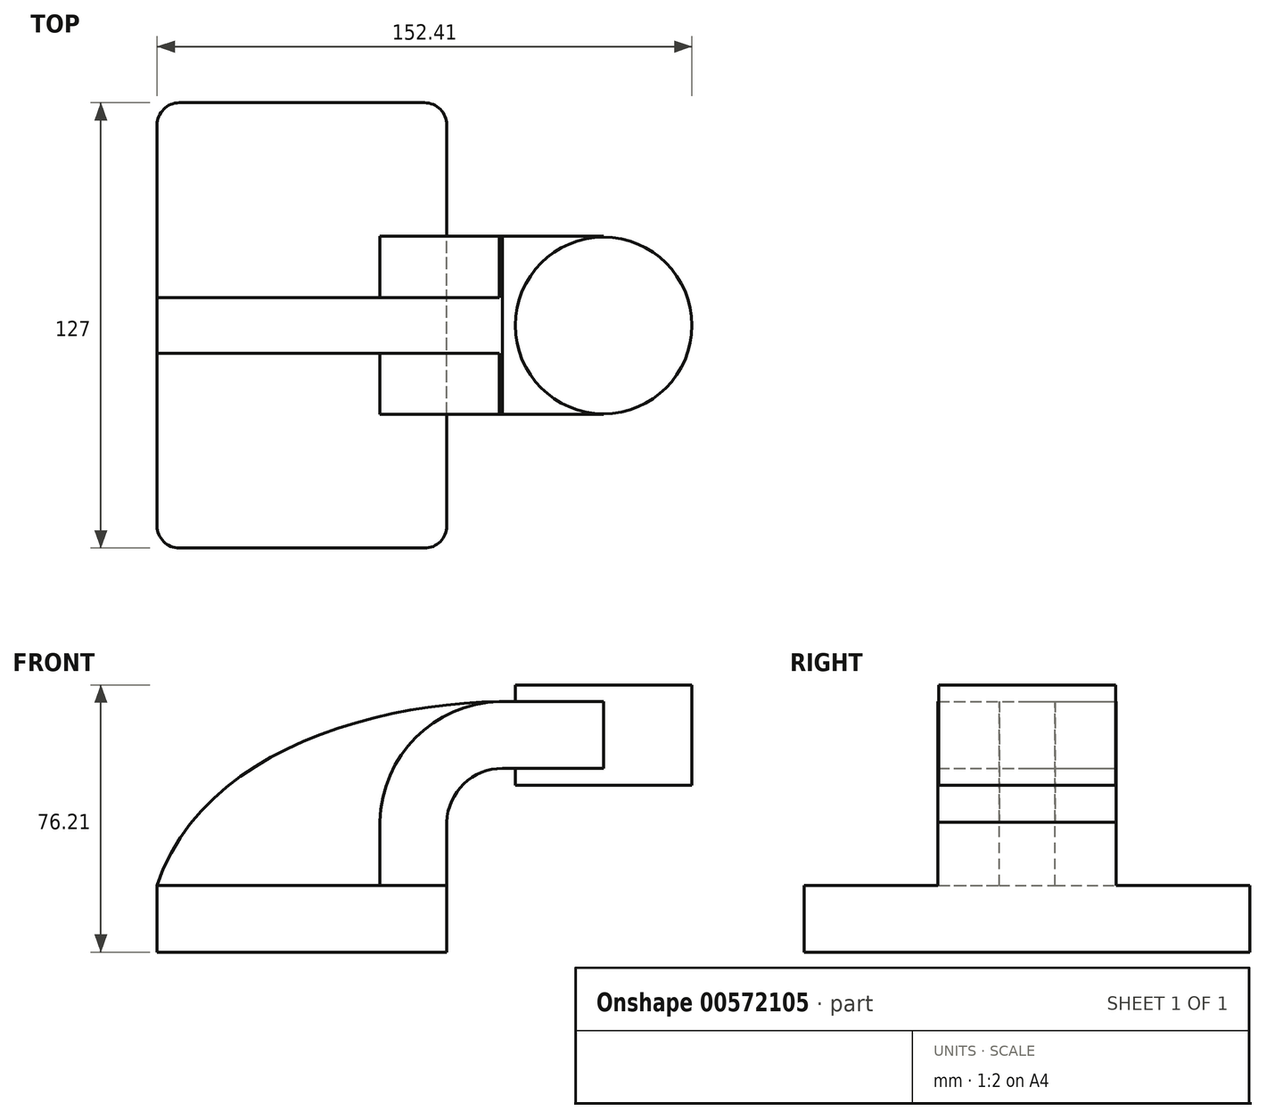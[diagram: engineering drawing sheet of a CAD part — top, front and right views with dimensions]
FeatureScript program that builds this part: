
annotation { "Feature Type Name" : "Feature", "Feature Type Description" : "" }
export const myFeature = defineFeature(function(context is Context, id is Id, definition is map)
    precondition{}
    {
        {
            var Q0;
            Q0=qCreatedBy(makeId("Front.planeOp"),FACE);
            var sketch = newSketch(context, id + "F0", { "sketchPlane" : qUnion([Q0])});
            skLineSegment(sketch, "E0.bottom", {"start": v(41.27, 9.53) * mm, "end": v(-41.28, 9.53) * mm});
            skLineSegment(sketch, "E0.top", {"start": v(41.28, -9.52) * mm, "end": v(-41.27, -9.53) * mm});
            skLineSegment(sketch, "E0.left", {"start": v(41.28, 9.53) * mm, "end": v(41.28, -9.52) * mm});
            skLineSegment(sketch, "E0.right", {"start": v(-41.28, 9.53) * mm, "end": v(-41.28, -9.53) * mm});
            skPoint(sketch, "E0.middle", {"position": v(0, 0) * mm});
            skLineSegment(sketch, "E1", {"start": v(41.27, 9.53) * mm, "end": v(41.27, 27.51) * mm});
            skLineSegment(sketch, "E2.bottom", {"start": v(60.32, 66.68) * mm, "end": v(111.12, 66.68) * mm});
            skLineSegment(sketch, "E2.top", {"start": v(60.32, 38.1) * mm, "end": v(111.12, 38.1) * mm});
            skLineSegment(sketch, "E2.left", {"start": v(60.32, 66.68) * mm, "end": v(60.32, 38.1) * mm});
            skLineSegment(sketch, "E2.right", {"start": v(111.12, 66.68) * mm, "end": v(111.12, 38.1) * mm});
            skPoint(sketch, "E2.middle", {"position": v(85.72, 52.39) * mm});
            skLineSegment(sketch, "E3", {"start": v(85.95, 42.88) * mm, "end": v(57.14, 42.88) * mm});
            skArc(sketch, "E4", {"start": v(57.14, 42.88) * mm, "mid": v(46.1, 38.4) * mm, "end": v(41.27, 27.51) * mm});
            skLineSegment(sketch, "E5.0", {"start": v(85.95, 61.93) * mm, "end": v(57.14, 61.93) * mm});
            skArc(sketch, "E5.1", {"start": v(57.14, 61.93) * mm, "mid": v(32.72, 51.96) * mm, "end": v(22.22, 27.76) * mm});
            skLineSegment(sketch, "E5.2", {"start": v(22.22, 9.53) * mm, "end": v(22.22, 27.76) * mm});
            skLineSegment(sketch, "E6", {"start": v(85.95, 38.1) * mm, "end": v(85.95, 66.68) * mm});
            skFitSpline(sketch, "E7", {"points": [v(-41.28, 9.53) * mm, v(57.14, 61.93) * mm], "startDerivative": vector(37.35, 113.1) * mm, "endDerivative": vector(112.88, 1.16) * mm});
            skSolve(sketch);
        }
        {
            var Q0;
            Q0=makeQuery(id+"F0.imprint","IMPRINT",FACE,{"disambiguationData":[TD([[makeQuery(id+"F0.imprint","IMPRINT",EDGE,{"derivedFrom":sQuery(id+"F0.wireOp",EDGE,"E0.top")}),-1.0]])]});
            extrude(context, id + "F1", {"entities" : qUnion([Q0]), "endBound" : BoundingType.SYMMETRIC, "depth" : 127 * mm, "offsetDistance" : 25.4 * mm});
        }
        {
            var Q0;
            {var subQ5=sQuery(id+"F0.wireOp",EDGE,"E1");Q0=makeQuery(id+"F0.imprint","IMPRINT",FACE,{"disambiguationData":[TD([[makeQuery(id+"F0.imprint","IMPRINT",EDGE,{"derivedFrom":subQ5}),1.0]])]});}
            var Q1;
            {var subQ0=sQuery(id+"F0.wireOp",EDGE,"E5.0");var subQ1=sQuery(id+"F0.wireOp",EDGE,"E2.left");var subQ2=makeQuery(id+"F0.imprint","INTERSECT",VERTEX,{"derivedFrom":[subQ1,subQ0]});Q1=makeQuery(id+"F0.imprint","IMPRINT",FACE,{"disambiguationData":[TD([[makeQuery(id+"F0.imprint","IMPRINT",EDGE,{"disambiguationData":[TD([[subQ2,-1.0]])],"derivedFrom":subQ1}),1.0]])]});}
            extrude(context, id + "F2", {"entities" : qUnion([Q0, Q1]), "operationType" : NewBodyOperationType.ADD, "endBound" : BoundingType.SYMMETRIC, "depth" : 50.8 * mm, "offsetDistance" : 25.4 * mm});
        }
        {
            var Q0;
            {var subQ3=sQuery(id+"F0.wireOp",EDGE,"E5.2");Q0=makeQuery(id+"F0.imprint","IMPRINT",FACE,{"disambiguationData":[TD([[makeQuery(id+"F0.imprint","IMPRINT",EDGE,{"derivedFrom":subQ3}),1.0]])]});}
            extrude(context, id + "F3", {"entities" : qUnion([Q0]), "operationType" : NewBodyOperationType.ADD, "endBound" : BoundingType.SYMMETRIC, "depth" : 15.88 * mm, "offsetDistance" : 25.4 * mm});
        }
        {
            var Q0;
            {var subQ0=sQuery(id+"F0.wireOp",EDGE,"E2.right");Q0=makeQuery(id+"F0.imprint","IMPRINT",FACE,{"disambiguationData":[TD([[makeQuery(id+"F0.imprint","IMPRINT",EDGE,{"derivedFrom":subQ0}),-1.0]])]});}
            var Q1;
            Q1=sQuery(id+"F0.wireOp",EDGE,"E6");
            revolve(context, id + "F4", {"operationType" : NewBodyOperationType.ADD, "entities" : qUnion([Q0]), "axis" : qUnion([Q1]), "revolveType" : RevolveType.FULL});
        }
        {
            var Q0;
            Q0=makeQuery(id+"F1.opExtrude","CAP_EDGE",EDGE,{"disambiguationData":[OSD([sQuery(id+"F0.wireOp",EDGE,"E0.left")])],"isStart":false});
            var Q1;
            Q1=makeQuery(id+"F1.opExtrude","CAP_EDGE",EDGE,{"disambiguationData":[OSD([sQuery(id+"F0.wireOp",EDGE,"E0.right")])],"isStart":false});
            var Q2;
            Q2=makeQuery(id+"F1.opExtrude","CAP_EDGE",EDGE,{"disambiguationData":[OSD([sQuery(id+"F0.wireOp",EDGE,"E0.left")])],"isStart":true});
            var Q3;
            Q3=makeQuery(id+"F1.opExtrude","CAP_EDGE",EDGE,{"disambiguationData":[OSD([sQuery(id+"F0.wireOp",EDGE,"E0.right")])],"isStart":true});
            fillet(context, id + "F5", {"entities" : qUnion([Q0, Q1, Q2, Q3]), "radius" : 6.35 * mm, "tangentPropagation" : true, "allowEdgeOverflow" : false});
        }
    });
